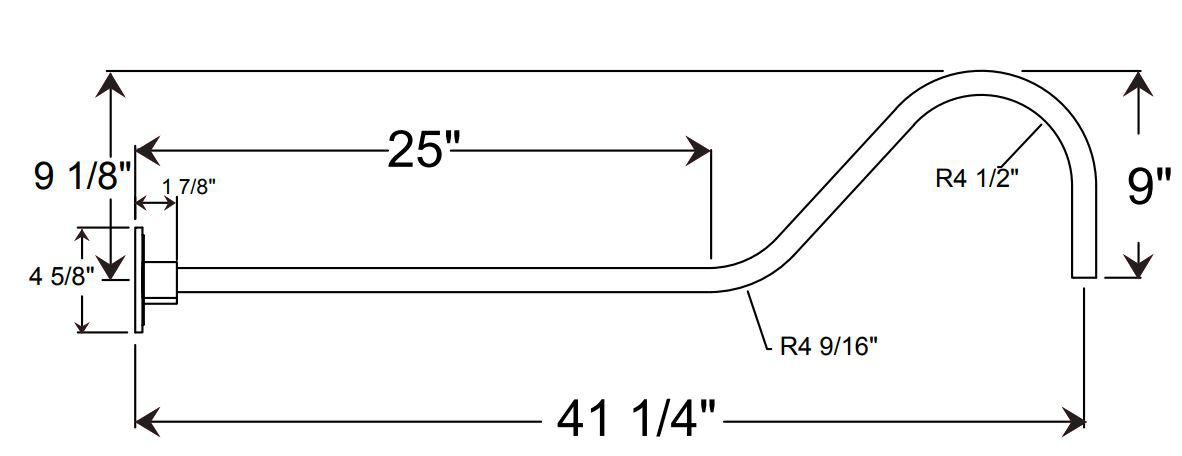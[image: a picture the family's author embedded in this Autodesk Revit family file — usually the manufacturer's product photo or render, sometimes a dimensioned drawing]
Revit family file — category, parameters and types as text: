
# Revit family: MILKCAN F(8,10,12,18) LED
name_source: partatom
category: Lighting Fixtures
units: mm (PartAtom-declared; Revit-internal decimal feet)

## family parameters
Always vertical = Yes
Cut with Voids When Loaded = No
Light Source = Yes
OmniClass Number = 23.80.70.00
OmniClass Title = Lighting
Part Type = Normal
Room Calculation Point = No
Round Connector Dimension = Use Diameter
Shared = No
Work Plane-Based = No

## types (4) — shared parameters
Body Colour = Spun aluminium
Body Material = body
CRI = >90
Color Filter = 16777215
Construction Material = Heavy Duty spun aluminum.
Default Elevation = 0' - 0"
Description = 120-277 Voltage
Dimming = 1%
Dimming Lamp Color Temperature Shift = <None>
Efficiency = 65-125 lumens per watt
Lamp = LED
Life = L70 50,000 hours
Load Classification = Lighting
Manufacturer = ANP Lighting
Photometric Web File = generic.ies
Power Factor = 1
Tilt Angle = 90.00°
URL = https://www.anplighting.com
Voltage = 277 V
Warranty = 5 year limited warranty

## per-type parameters (varying)
| type | Apparent Load | Fixture Diameter | Fixture Height | MCF08 | MCF10 | MCF12 | MCF18 | Wattage Comments | Weight |
| MCF08 | 9 VA | 0' - 8" | 0' - 4" | Yes | No | No | No | 9W | 1 lbs |
| MCF10 | 10 VA | 0' - 10" | 0' - 4" | No | Yes | No | No | 10W | 1 lbs |
| MCF12 | 16 VA | 1' - 0" | 0' - 5" | No | No | Yes | No | 16W | 1.5 lbs |
| MCF18 | 24 VA | 0' - 6" | 1' - 6" | No | No | No | Yes | 24W | 2 lbs |

note: column(s) folded — value = type name in every type: Model

## geometry (parser evidence)
native form markers: Sweep x32
no freeform markers — native parametric forms only
